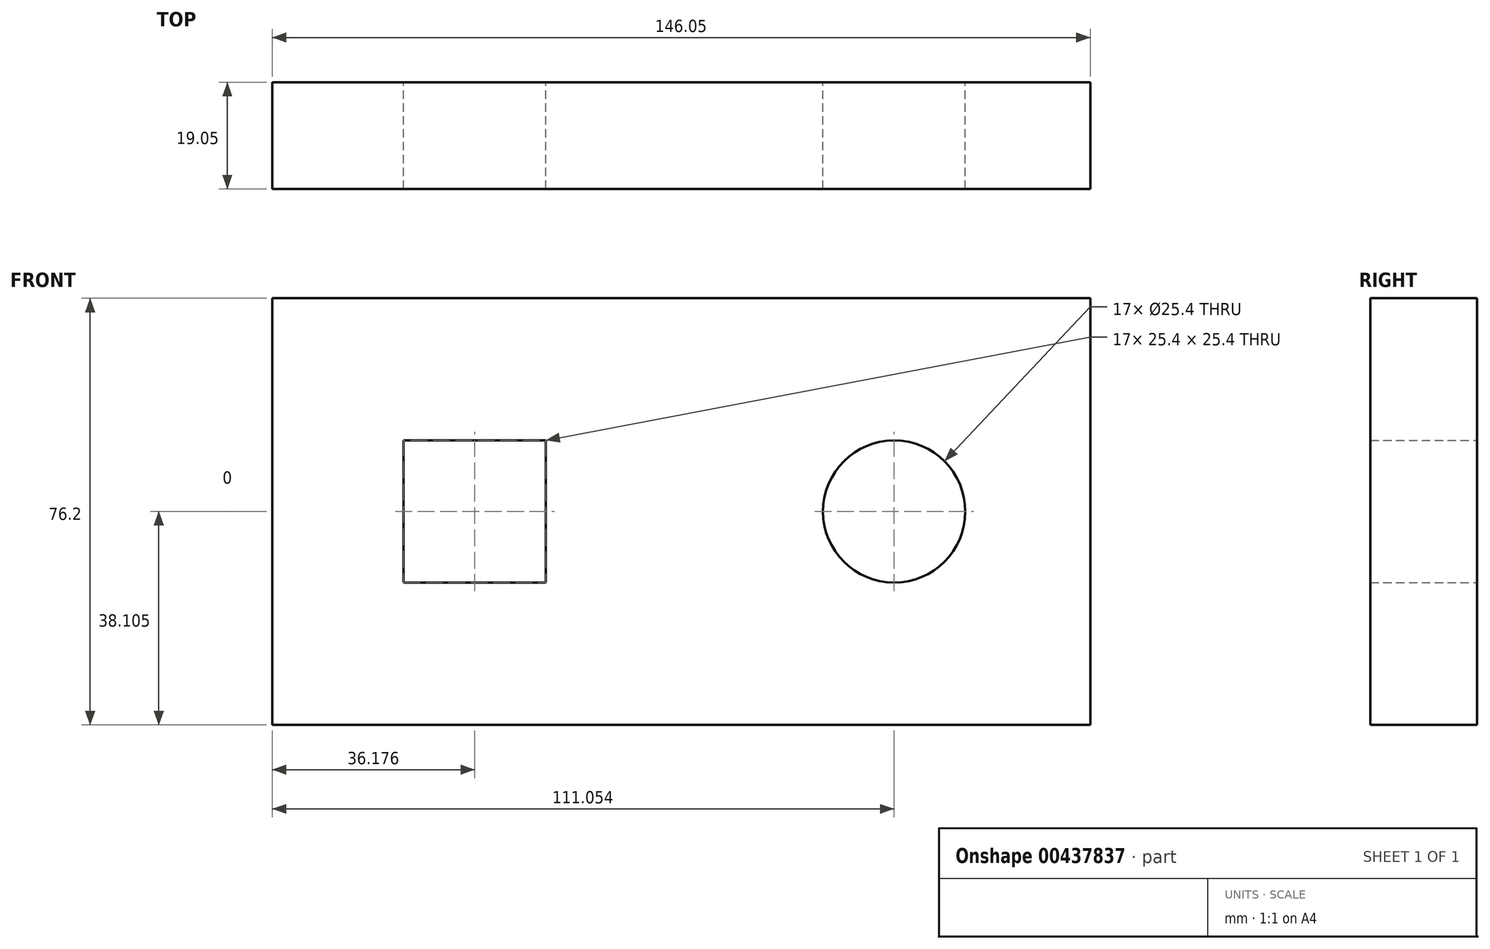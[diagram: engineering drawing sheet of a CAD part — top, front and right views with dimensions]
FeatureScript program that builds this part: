
annotation { "Feature Type Name" : "Feature", "Feature Type Description" : "" }
export const myFeature = defineFeature(function(context is Context, id is Id, definition is map)
    precondition{}
    {
        {
            var Q0;
            Q0=qCreatedBy(makeId("Front.planeOp"),FACE);
            var sketch = newSketch(context, id + "F0", { "sketchPlane" : qUnion([Q0])});
            skLineSegment(sketch, "E0.bottom", {"start": v(74.5, 10.63) * mm, "end": v(-71.55, 10.63) * mm});
            skLineSegment(sketch, "E0.top", {"start": v(74.5, -65.57) * mm, "end": v(-71.55, -65.57) * mm});
            skLineSegment(sketch, "E0.left", {"start": v(74.5, 10.63) * mm, "end": v(74.5, -65.57) * mm});
            skLineSegment(sketch, "E0.right", {"start": v(-71.55, 10.63) * mm, "end": v(-71.55, -65.57) * mm});
            skCircle(sketch, "E1", {"center": v(39.5, -27.47) * mm, "radius": 12.7 * mm});
            skLineSegment(sketch, "E2.left", {"start": v(-48.07, -27.47) * mm, "end": v(-48.07, -20.43) * mm});
            skLineSegment(sketch, "E3", {"start": v(-48.07, -27.47) * mm, "end": v(-48.07, -40.17) * mm});
            skLineSegment(sketch, "E4", {"start": v(-48.07, -40.17) * mm, "end": v(-22.67, -40.17) * mm});
            skLineSegment(sketch, "E5", {"start": v(-22.67, -40.17) * mm, "end": v(-22.67, -27.47) * mm});
            skLineSegment(sketch, "E6", {"start": v(-22.67, -27.47) * mm, "end": v(-22.67, -14.77) * mm});
            skLineSegment(sketch, "E7", {"start": v(-22.67, -14.77) * mm, "end": v(-48.07, -14.77) * mm});
            skLineSegment(sketch, "E8", {"start": v(-48.07, -14.77) * mm, "end": v(-48.07, -20.43) * mm});
            skPoint(sketch, "E9.orphan", {"position": v(1.48, 10.63) * mm});
            skPoint(sketch, "E10.end.orphan", {"position": v(1.48, -65.57) * mm});
            skPoint(sketch, "E11.orphan", {"position": v(74.5, -27.47) * mm});
            skPoint(sketch, "E12.orphan", {"position": v(-71.55, -27.47) * mm});
            skSolve(sketch);
        }
        {
            var Q0;
            Q0 = qSketchRegion(id + "F0", true);
            extrude(context, id + "F1", {"entities" : qUnion([Q0]), "depth" : 19.05 * mm});
        }
    });
